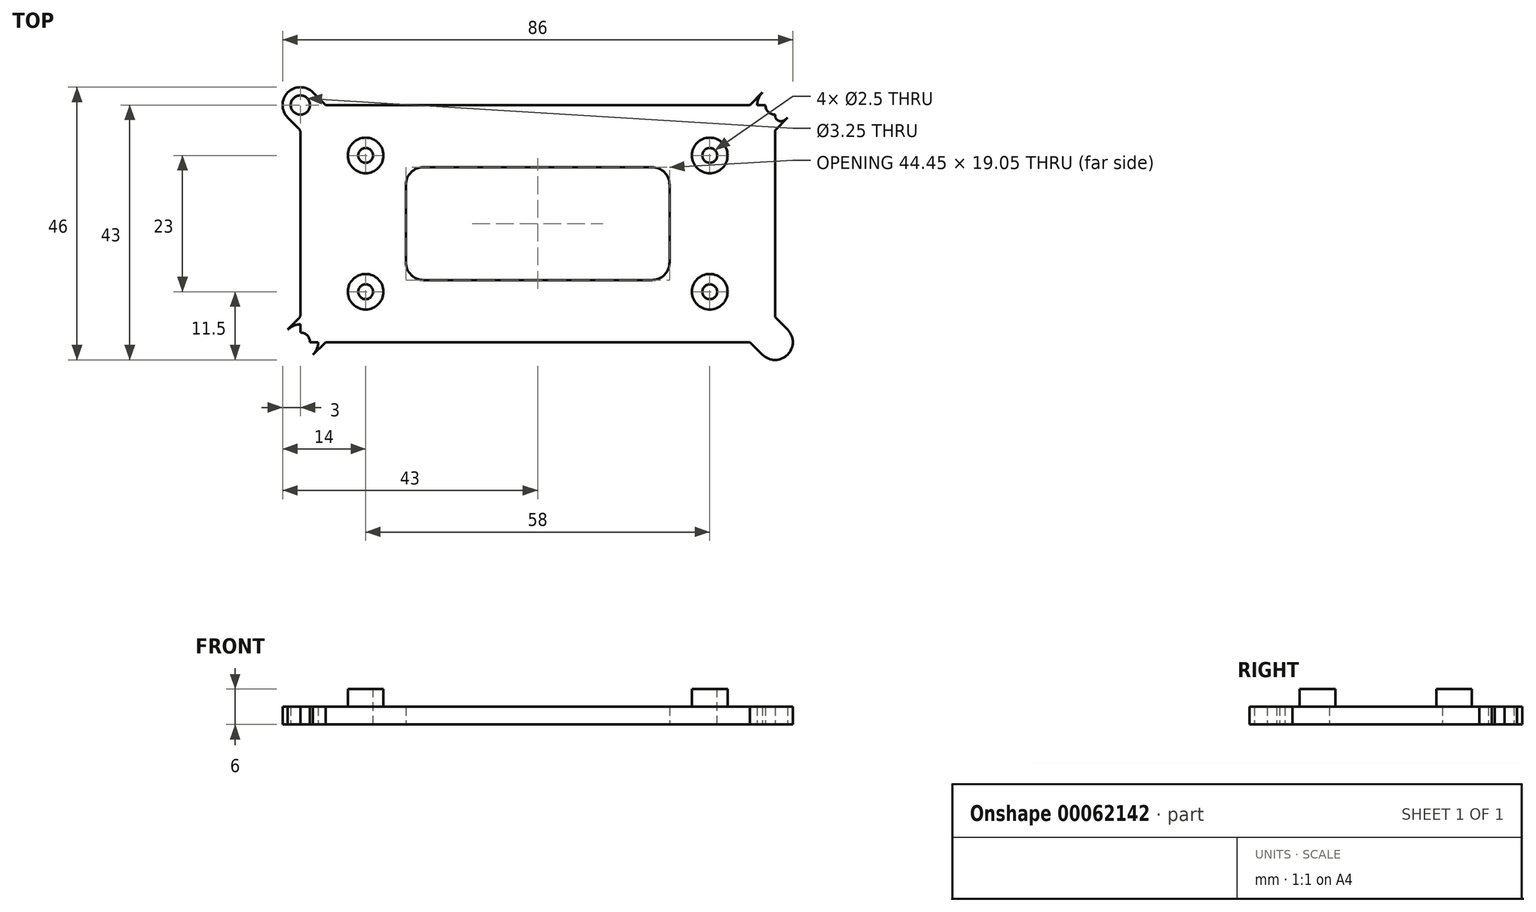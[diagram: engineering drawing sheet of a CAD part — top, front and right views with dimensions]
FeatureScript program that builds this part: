
annotation { "Feature Type Name" : "Feature", "Feature Type Description" : "" }
export const myFeature = defineFeature(function(context is Context, id is Id, definition is map)
    precondition{}
    {
        {
            var Q0;
            Q0=qCreatedBy(makeId("Top.planeOp"),FACE);
            var sketch = newSketch(context, id + "F0", { "sketchPlane" : qUnion([Q0])});
            skLineSegment(sketch, "E0.bottom", {"start": v(-40, 20) * mm, "end": v(40, 20) * mm});
            skLineSegment(sketch, "E0.top", {"start": v(-40, -20) * mm, "end": v(40, -20) * mm});
            skLineSegment(sketch, "E0.left", {"start": v(-40, 20) * mm, "end": v(-40, -20) * mm});
            skLineSegment(sketch, "E0.right", {"start": v(40, 20) * mm, "end": v(40, -20) * mm});
            skSolve(sketch);
        }
        {
            var Q0;
            Q0=makeQuery(id+"F0.imprint","IMPRINT",FACE,{"disambiguationData":[TD([[makeQuery(id+"F0.imprint","IMPRINT",EDGE,{"derivedFrom":sQuery(id+"F0.wireOp",EDGE,"E0.bottom")}),-1.0]])]});
            extrude(context, id + "F1", {"entities" : qUnion([Q0]), "depth" : 3 * mm});
        }
        {
            var Q0;
            Q0=makeQuery(id+"F1.opExtrude","CAP_FACE",FACE,{"disambiguationData":[OSD([sQuery(id+"F0.wireOp",EDGE,"E0.bottom"),sQuery(id+"F0.wireOp",EDGE,"E0.top"),sQuery(id+"F0.wireOp",EDGE,"E0.left"),sQuery(id+"F0.wireOp",EDGE,"E0.right")])],"isStart":false});
            var sketch = newSketch(context, id + "F2", { "sketchPlane" : qUnion([Q0])});
            skCircle(sketch, "E1", {"center": v(-29, -11.5) * mm, "radius": 3 * mm});
            skCircle(sketch, "E2", {"center": v(29, -11.5) * mm, "radius": 3 * mm});
            skCircle(sketch, "E3", {"center": v(29, 11.5) * mm, "radius": 3 * mm});
            skCircle(sketch, "E4", {"center": v(-29, 11.5) * mm, "radius": 3 * mm});
            skSolve(sketch);
        }
        {
            var Q0;
            Q0=makeQuery(id+"F2.imprint","IMPRINT",FACE,{"disambiguationData":[TD([[makeQuery(id+"F2.imprint","IMPRINT",EDGE,{"derivedFrom":sQuery(id+"F2.wireOp",EDGE,"E4")}),1.0]])]});
            var Q1;
            Q1=makeQuery(id+"F2.imprint","IMPRINT",FACE,{"disambiguationData":[TD([[makeQuery(id+"F2.imprint","IMPRINT",EDGE,{"derivedFrom":sQuery(id+"F2.wireOp",EDGE,"E3")}),1.0]])]});
            var Q2;
            Q2=makeQuery(id+"F2.imprint","IMPRINT",FACE,{"disambiguationData":[TD([[makeQuery(id+"F2.imprint","IMPRINT",EDGE,{"derivedFrom":sQuery(id+"F2.wireOp",EDGE,"E2")}),1.0]])]});
            var Q3;
            Q3=makeQuery(id+"F2.imprint","IMPRINT",FACE,{"disambiguationData":[TD([[makeQuery(id+"F2.imprint","IMPRINT",EDGE,{"derivedFrom":sQuery(id+"F2.wireOp",EDGE,"E1")}),1.0]])]});
            extrude(context, id + "F3", {"entities" : qUnion([Q0, Q1, Q2, Q3]), "operationType" : NewBodyOperationType.ADD, "depth" : 3 * mm});
        }
        {
            var Q0;
            Q0=makeQuery(id+"F3.opExtrude","CAP_FACE",FACE,{"disambiguationData":[OSD([sQuery(id+"F2.wireOp",EDGE,"E3")])],"isStart":false});
            var sketch = newSketch(context, id + "F4", { "sketchPlane" : qUnion([Q0])});
            skCircle(sketch, "E5.0", {"center": v(-29, 11.5) * mm, "radius": 3 * mm});
            skCircle(sketch, "E5.1", {"center": v(29, 11.5) * mm, "radius": 3 * mm});
            skCircle(sketch, "E5.2", {"center": v(29, -11.5) * mm, "radius": 3 * mm});
            skCircle(sketch, "E5.3", {"center": v(-29, -11.5) * mm, "radius": 3 * mm});
            skSolve(sketch);
        }
        {
            var Q0;
            Q0=sQuery(id+"F4.wireOp",VERTEX,"E5.0.center");
            var Q1;
            Q1=sQuery(id+"F4.wireOp",VERTEX,"E5.1.center");
            var Q2;
            Q2=sQuery(id+"F4.wireOp",VERTEX,"E5.2.center");
            var Q3;
            Q3=sQuery(id+"F4.wireOp",VERTEX,"E5.3.center");
            var Q4;
            Q4=makeQuery(id+"F1.opExtrude","SWEPT_BODY",BODY,{"disambiguationData":[OSD([sQuery(id+"F0.wireOp",EDGE,"E0.bottom"),sQuery(id+"F0.wireOp",EDGE,"E0.top"),sQuery(id+"F0.wireOp",EDGE,"E0.left"),sQuery(id+"F0.wireOp",EDGE,"E0.right")])]});
            hole(context, id + "F5", {"style" : HoleStyle.SIMPLE, "holeDiameter" : 2.5 * mm, "endStyle" : HoleEndStyle.THROUGH, "locations" : qUnion([Q0, Q1, Q2, Q3]), "scope" : qUnion([Q4])});
        }
        {
            var Q0;
            Q0=makeQuery(id+"F1.opExtrude","CAP_FACE",FACE,{"disambiguationData":[OSD([sQuery(id+"F0.wireOp",EDGE,"E0.bottom"),sQuery(id+"F0.wireOp",EDGE,"E0.top"),sQuery(id+"F0.wireOp",EDGE,"E0.left"),sQuery(id+"F0.wireOp",EDGE,"E0.right")])],"isStart":true});
            var sketch = newSketch(context, id + "F6", { "sketchPlane" : qUnion([Q0])});
            skCircle(sketch, "E6", {"center": v(40, 20) * mm, "radius": 3 * mm});
            skLineSegment(sketch, "E7", {"start": v(37.88, 22.12) * mm, "end": v(35.76, 20) * mm});
            skLineSegment(sketch, "E8", {"start": v(42.12, 17.88) * mm, "end": v(40, 15.76) * mm});
            skLineSegment(sketch, "E9.MirrorCS", {"start": v(37.88, -22.12) * mm, "end": v(35.76, -20) * mm});
            skLineSegment(sketch, "E10.MirrorCS", {"start": v(42.12, -17.88) * mm, "end": v(40, -15.76) * mm});
            skCircle(sketch, "E11.MirrorC", {"center": v(40, -20) * mm, "radius": 3 * mm});
            skLineSegment(sketch, "E12.MirrorCS", {"start": v(-37.88, -22.12) * mm, "end": v(-35.76, -20) * mm});
            skCircle(sketch, "E13.MirrorC", {"center": v(-40, -20) * mm, "radius": 3 * mm});
            skLineSegment(sketch, "E14.MirrorCS", {"start": v(-42.12, -17.88) * mm, "end": v(-40, -15.76) * mm});
            skLineSegment(sketch, "E15.MirrorCS", {"start": v(-42.12, 17.88) * mm, "end": v(-40, 15.76) * mm});
            skLineSegment(sketch, "E16.MirrorCS", {"start": v(-37.88, 22.12) * mm, "end": v(-35.76, 20) * mm});
            skCircle(sketch, "E17.MirrorC", {"center": v(-40, 20) * mm, "radius": 3 * mm});
            skSolve(sketch);
        }
        {
            var Q0;
            {var subQ0=sQuery(id+"F6.wireOp",EDGE,"E6");var subQ1=makeQuery(id+"F6.imprint","INTERSECT",VERTEX,{"derivedFrom":[subQ0,sQuery(id+"F6.wireOp",EDGE,"soFXJ1EB-8HO6-MR9N-8HIc-to1pPQWrAkPu")]});Q0=makeQuery(id+"F6.imprint","IMPRINT",FACE,{"disambiguationData":[TD([[makeQuery(id+"F6.imprint","IMPRINT",EDGE,{"disambiguationData":[TD([[subQ1,-1.0]])],"derivedFrom":subQ0}),1.0]])]});}
            var Q1;
            {var subQ0=sQuery(id+"F6.wireOp",EDGE,"soFXJ1EB-8HO6-MR9N-8HIc-to1pPQWrAkPu");Q1=makeQuery(id+"F6.imprint","IMPRINT",FACE,{"disambiguationData":[TD([[makeQuery(id+"F6.imprint","IMPRINT",EDGE,{"derivedFrom":subQ0}),1.0]])]});}
            var Q2;
            {var subQ0=sQuery(id+"F6.wireOp",EDGE,"Z4YqX5LU-mUXy-Cds5-Czo9-QNd9TRQbJKcO");Q2=makeQuery(id+"F6.imprint","IMPRINT",FACE,{"disambiguationData":[TD([[makeQuery(id+"F6.imprint","IMPRINT",EDGE,{"derivedFrom":subQ0}),-1.0]])]});}
            var Q3;
            {var subQ0=sQuery(id+"F6.wireOp",EDGE,"a5341563-2c41-44e3-9b47-e9f27f0d3a280.MirrorC");var subQ1=makeQuery(id+"F6.imprint","INTERSECT",VERTEX,{"derivedFrom":[sQuery(id+"F6.wireOp",EDGE,"0210edd8-b347-4c23-a09a-b419c3a22fa00.MirrorCS"),subQ0]});Q3=makeQuery(id+"F6.imprint","IMPRINT",FACE,{"disambiguationData":[TD([[makeQuery(id+"F6.imprint","IMPRINT",EDGE,{"disambiguationData":[TD([[subQ1,-1.0]])],"derivedFrom":subQ0}),-1.0]])]});}
            var Q4;
            {var subQ0=sQuery(id+"F6.wireOp",EDGE,"0210edd8-b347-4c23-a09a-b419c3a22fa00.MirrorCS");Q4=makeQuery(id+"F6.imprint","IMPRINT",FACE,{"disambiguationData":[TD([[makeQuery(id+"F6.imprint","IMPRINT",EDGE,{"derivedFrom":subQ0}),-1.0]])]});}
            var Q5;
            {var subQ0=sQuery(id+"F6.wireOp",EDGE,"2f044340-a0b1-4631-b95b-f2c242ba9c770.MirrorCS");Q5=makeQuery(id+"F6.imprint","IMPRINT",FACE,{"disambiguationData":[TD([[makeQuery(id+"F6.imprint","IMPRINT",EDGE,{"derivedFrom":subQ0}),1.0]])]});}
            var Q6;
            {var subQ0=sQuery(id+"F6.wireOp",EDGE,"2f99d0b1-1a89-4974-9a16-afa06d6dc4af0.MirrorC");var subQ1=makeQuery(id+"F6.imprint","INTERSECT",VERTEX,{"derivedFrom":[subQ0,sQuery(id+"F6.wireOp",EDGE,"bc17fd96-254d-4ff9-a344-3499c0479a8f0.MirrorCS")]});Q6=makeQuery(id+"F6.imprint","IMPRINT",FACE,{"disambiguationData":[TD([[makeQuery(id+"F6.imprint","IMPRINT",EDGE,{"disambiguationData":[TD([[subQ1,-1.0]])],"derivedFrom":subQ0}),1.0]])]});}
            var Q7;
            {var subQ0=sQuery(id+"F6.wireOp",EDGE,"f0ec589f-6775-499c-a41f-7fb6111fc43a0.MirrorCS");Q7=makeQuery(id+"F6.imprint","IMPRINT",FACE,{"disambiguationData":[TD([[makeQuery(id+"F6.imprint","IMPRINT",EDGE,{"derivedFrom":subQ0}),-1.0]])]});}
            var Q8;
            {var subQ0=sQuery(id+"F6.wireOp",EDGE,"bc17fd96-254d-4ff9-a344-3499c0479a8f0.MirrorCS");Q8=makeQuery(id+"F6.imprint","IMPRINT",FACE,{"disambiguationData":[TD([[makeQuery(id+"F6.imprint","IMPRINT",EDGE,{"derivedFrom":subQ0}),1.0]])]});}
            var Q9;
            {var subQ0=sQuery(id+"F6.wireOp",EDGE,"94c3390e-faa4-4edb-91fe-58140658a5c30.MirrorC");var subQ1=makeQuery(id+"F6.imprint","INTERSECT",VERTEX,{"derivedFrom":[subQ0,sQuery(id+"F6.wireOp",EDGE,"4ec94b05-feb2-45ef-b047-bc99985147690.MirrorCS")]});Q9=makeQuery(id+"F6.imprint","IMPRINT",FACE,{"disambiguationData":[TD([[makeQuery(id+"F6.imprint","IMPRINT",EDGE,{"disambiguationData":[TD([[subQ1,-1.0]])],"derivedFrom":subQ0}),-1.0]])]});}
            var Q10;
            {var subQ0=sQuery(id+"F6.wireOp",EDGE,"213ae7a3-055c-491c-8cde-c86d012d92890.MirrorCS");Q10=makeQuery(id+"F6.imprint","IMPRINT",FACE,{"disambiguationData":[TD([[makeQuery(id+"F6.imprint","IMPRINT",EDGE,{"derivedFrom":subQ0}),1.0]])]});}
            var Q11;
            {var subQ0=sQuery(id+"F6.wireOp",EDGE,"4ec94b05-feb2-45ef-b047-bc99985147690.MirrorCS");Q11=makeQuery(id+"F6.imprint","IMPRINT",FACE,{"disambiguationData":[TD([[makeQuery(id+"F6.imprint","IMPRINT",EDGE,{"derivedFrom":subQ0}),-1.0]])]});}
            var Q12;
            {var subQ3=sQuery(id+"F6.wireOp",EDGE,"E17.MirrorC");var subQ6=makeQuery(id+"F6.imprint","INTERSECT",VERTEX,{"derivedFrom":[sQuery(id+"F6.wireOp",EDGE,"E16.MirrorCS"),subQ3]});Q12=makeQuery(id+"F6.imprint","IMPRINT",FACE,{"disambiguationData":[TD([[makeQuery(id+"F6.imprint","IMPRINT",EDGE,{"disambiguationData":[TD([[subQ6,-1.0]])],"derivedFrom":subQ3}),-1.0]])]});}
            var Q13;
            {var subQ0=sQuery(id+"F6.wireOp",EDGE,"E16.MirrorCS");Q13=makeQuery(id+"F6.imprint","IMPRINT",FACE,{"disambiguationData":[TD([[makeQuery(id+"F6.imprint","IMPRINT",EDGE,{"derivedFrom":subQ0}),-1.0]])]});}
            var Q14;
            {var subQ0=sQuery(id+"F6.wireOp",EDGE,"E15.MirrorCS");Q14=makeQuery(id+"F6.imprint","IMPRINT",FACE,{"disambiguationData":[TD([[makeQuery(id+"F6.imprint","IMPRINT",EDGE,{"derivedFrom":subQ0}),1.0]])]});}
            var Q15;
            {var subQ0=sQuery(id+"F6.wireOp",EDGE,"E13.MirrorC");var subQ1=makeQuery(id+"F6.imprint","INTERSECT",VERTEX,{"derivedFrom":[sQuery(id+"F6.wireOp",EDGE,"E12.MirrorCS"),subQ0]});Q15=makeQuery(id+"F6.imprint","IMPRINT",FACE,{"disambiguationData":[TD([[makeQuery(id+"F6.imprint","IMPRINT",EDGE,{"disambiguationData":[TD([[subQ1,-1.0]])],"derivedFrom":subQ0}),1.0]])]});}
            var Q16;
            {var subQ0=sQuery(id+"F6.wireOp",EDGE,"E14.MirrorCS");Q16=makeQuery(id+"F6.imprint","IMPRINT",FACE,{"disambiguationData":[TD([[makeQuery(id+"F6.imprint","IMPRINT",EDGE,{"derivedFrom":subQ0}),-1.0]])]});}
            var Q17;
            {var subQ0=sQuery(id+"F6.wireOp",EDGE,"E12.MirrorCS");Q17=makeQuery(id+"F6.imprint","IMPRINT",FACE,{"disambiguationData":[TD([[makeQuery(id+"F6.imprint","IMPRINT",EDGE,{"derivedFrom":subQ0}),1.0]])]});}
            var Q18;
            {var subQ3=sQuery(id+"F6.wireOp",EDGE,"E11.MirrorC");var subQ7=makeQuery(id+"F6.imprint","INTERSECT",VERTEX,{"derivedFrom":[sQuery(id+"F6.wireOp",EDGE,"E9.MirrorCS"),subQ3]});Q18=makeQuery(id+"F6.imprint","IMPRINT",FACE,{"disambiguationData":[TD([[makeQuery(id+"F6.imprint","IMPRINT",EDGE,{"disambiguationData":[TD([[subQ7,-1.0]])],"derivedFrom":subQ3}),-1.0]])]});}
            var Q19;
            {var subQ0=sQuery(id+"F6.wireOp",EDGE,"E10.MirrorCS");Q19=makeQuery(id+"F6.imprint","IMPRINT",FACE,{"disambiguationData":[TD([[makeQuery(id+"F6.imprint","IMPRINT",EDGE,{"derivedFrom":subQ0}),1.0]])]});}
            var Q20;
            {var subQ0=sQuery(id+"F6.wireOp",EDGE,"E9.MirrorCS");Q20=makeQuery(id+"F6.imprint","IMPRINT",FACE,{"disambiguationData":[TD([[makeQuery(id+"F6.imprint","IMPRINT",EDGE,{"derivedFrom":subQ0}),-1.0]])]});}
            var Q21;
            {var subQ0=sQuery(id+"F6.wireOp",EDGE,"E8");Q21=makeQuery(id+"F6.imprint","IMPRINT",FACE,{"disambiguationData":[TD([[makeQuery(id+"F6.imprint","IMPRINT",EDGE,{"derivedFrom":subQ0}),-1.0]])]});}
            var Q22;
            {var subQ0=sQuery(id+"F6.wireOp",EDGE,"E7");Q22=makeQuery(id+"F6.imprint","IMPRINT",FACE,{"disambiguationData":[TD([[makeQuery(id+"F6.imprint","IMPRINT",EDGE,{"derivedFrom":subQ0}),1.0]])]});}
            extrude(context, id + "F7", {"entities" : qUnion([Q0, Q1, Q2, Q3, Q4, Q5, Q6, Q7, Q8, Q9, Q10, Q11, Q12, Q13, Q14, Q15, Q16, Q17, Q18, Q19, Q20, Q21, Q22]), "operationType" : NewBodyOperationType.ADD, "oppositeDirection" : true, "depth" : 3 * mm});
        }
        {
            var Q0;
            {var subQ0=sQuery(id+"F0.wireOp",EDGE,"E0.left");var subQ1=sQuery(id+"F0.wireOp",EDGE,"E0.right");Q0=makeQuery(id+"F7.boolean.opBoolean","MERGE",FACE,{"derivedFrom":[makeQuery(id+"F1.opExtrude","CAP_FACE",FACE,{"disambiguationData":[OSD([sQuery(id+"F0.wireOp",EDGE,"E0.bottom"),sQuery(id+"F0.wireOp",EDGE,"E0.top"),subQ0,subQ1])],"isStart":true}),makeQuery(id+"F7.opExtrude","CAP_FACE",FACE,{"disambiguationData":[OSD([subQ1,sQuery(id+"F6.wireOp",EDGE,"E6"),sQuery(id+"F6.wireOp",EDGE,"soFXJ1EB-8HO6-MR9N-8HIc-to1pPQWrAkPu"),sQuery(id+"F6.wireOp",EDGE,"Z4YqX5LU-mUXy-Cds5-Czo9-QNd9TRQbJKcO")])],"isStart":true}),makeQuery(id+"F7.opExtrude","CAP_FACE",FACE,{"disambiguationData":[OSD([subQ1,sQuery(id+"F6.wireOp",EDGE,"213ae7a3-055c-491c-8cde-c86d012d92890.MirrorCS"),sQuery(id+"F6.wireOp",EDGE,"94c3390e-faa4-4edb-91fe-58140658a5c30.MirrorC"),sQuery(id+"F6.wireOp",EDGE,"4ec94b05-feb2-45ef-b047-bc99985147690.MirrorCS")])],"isStart":true}),makeQuery(id+"F7.opExtrude","CAP_FACE",FACE,{"disambiguationData":[OSD([subQ0,sQuery(id+"F6.wireOp",EDGE,"0210edd8-b347-4c23-a09a-b419c3a22fa00.MirrorCS"),sQuery(id+"F6.wireOp",EDGE,"2f044340-a0b1-4631-b95b-f2c242ba9c770.MirrorCS"),sQuery(id+"F6.wireOp",EDGE,"a5341563-2c41-44e3-9b47-e9f27f0d3a280.MirrorC")])],"isStart":true}),makeQuery(id+"F7.opExtrude","CAP_FACE",FACE,{"disambiguationData":[OSD([subQ0,sQuery(id+"F6.wireOp",EDGE,"f0ec589f-6775-499c-a41f-7fb6111fc43a0.MirrorCS"),sQuery(id+"F6.wireOp",EDGE,"2f99d0b1-1a89-4974-9a16-afa06d6dc4af0.MirrorC"),sQuery(id+"F6.wireOp",EDGE,"bc17fd96-254d-4ff9-a344-3499c0479a8f0.MirrorCS")])],"isStart":true})]});}
            var sketch = newSketch(context, id + "F8", { "sketchPlane" : qUnion([Q0])});
            skLineSegment(sketch, "E18.3", {"start": v(37.88, 22.12) * mm, "end": v(37.88, 22.12) * mm});
            skArc(sketch, "E19.0", {"start": v(-42.12, 17.88) * mm, "mid": v(-42.12, 22.12) * mm, "end": v(-37.88, 22.12) * mm});
            skArc(sketch, "E19.1", {"start": v(-42.12, -17.88) * mm, "mid": v(-42.12, -22.12) * mm, "end": v(-37.88, -22.12) * mm});
            skArc(sketch, "E19.2", {"start": v(42.12, -17.88) * mm, "mid": v(42.12, -22.12) * mm, "end": v(37.88, -22.12) * mm});
            skSolve(sketch);
        }
        {
            var Q0;
            Q0=sQuery(id+"F8.wireOp",VERTEX,"E18.0.center");
            var Q1;
            Q1=sQuery(id+"F8.wireOp",VERTEX,"E18.1.center");
            var Q2;
            Q2=sQuery(id+"F8.wireOp",VERTEX,"E18.2.center");
            var Q3;
            Q3=sQuery(id+"F8.wireOp",VERTEX,"E18.3.center");
            var Q4;
            Q4=sQuery(id+"F8.wireOp",VERTEX,"E19.0.center");
            var Q5;
            Q5=sQuery(id+"F8.wireOp",VERTEX,"E19.1.center");
            var Q6;
            Q6=sQuery(id+"F8.wireOp",VERTEX,"E19.2.center");
            var Q7;
            Q7=makeQuery(id+"F1.opExtrude","SWEPT_BODY",BODY,{"disambiguationData":[OSD([sQuery(id+"F0.wireOp",EDGE,"E0.bottom"),sQuery(id+"F0.wireOp",EDGE,"E0.top"),sQuery(id+"F0.wireOp",EDGE,"E0.left"),sQuery(id+"F0.wireOp",EDGE,"E0.right")])]});
            hole(context, id + "F9", {"style" : HoleStyle.SIMPLE, "holeDiameter" : 3.25 * mm, "endStyle" : HoleEndStyle.THROUGH, "locations" : qUnion([Q0, Q1, Q2, Q3, Q4, Q5, Q6]), "scope" : qUnion([Q7])});
        }
        {
            var Q0;
            {var subQ0=sQuery(id+"F0.wireOp",EDGE,"E0.left");var subQ1=sQuery(id+"F0.wireOp",EDGE,"E0.right");Q0=makeQuery(id+"F7.boolean.opBoolean","MERGE",FACE,{"derivedFrom":[makeQuery(id+"F1.opExtrude","CAP_FACE",FACE,{"disambiguationData":[OSD([sQuery(id+"F0.wireOp",EDGE,"E0.bottom"),sQuery(id+"F0.wireOp",EDGE,"E0.top"),subQ0,subQ1])],"isStart":true}),makeQuery(id+"F7.opExtrude","CAP_FACE",FACE,{"disambiguationData":[OSD([subQ1,sQuery(id+"F6.wireOp",EDGE,"E6"),sQuery(id+"F6.wireOp",EDGE,"soFXJ1EB-8HO6-MR9N-8HIc-to1pPQWrAkPu"),sQuery(id+"F6.wireOp",EDGE,"Z4YqX5LU-mUXy-Cds5-Czo9-QNd9TRQbJKcO")])],"isStart":true}),makeQuery(id+"F7.opExtrude","CAP_FACE",FACE,{"disambiguationData":[OSD([subQ1,sQuery(id+"F6.wireOp",EDGE,"213ae7a3-055c-491c-8cde-c86d012d92890.MirrorCS"),sQuery(id+"F6.wireOp",EDGE,"94c3390e-faa4-4edb-91fe-58140658a5c30.MirrorC"),sQuery(id+"F6.wireOp",EDGE,"4ec94b05-feb2-45ef-b047-bc99985147690.MirrorCS")])],"isStart":true}),makeQuery(id+"F7.opExtrude","CAP_FACE",FACE,{"disambiguationData":[OSD([subQ0,sQuery(id+"F6.wireOp",EDGE,"0210edd8-b347-4c23-a09a-b419c3a22fa00.MirrorCS"),sQuery(id+"F6.wireOp",EDGE,"2f044340-a0b1-4631-b95b-f2c242ba9c770.MirrorCS"),sQuery(id+"F6.wireOp",EDGE,"a5341563-2c41-44e3-9b47-e9f27f0d3a280.MirrorC")])],"isStart":true}),makeQuery(id+"F7.opExtrude","CAP_FACE",FACE,{"disambiguationData":[OSD([subQ0,sQuery(id+"F6.wireOp",EDGE,"f0ec589f-6775-499c-a41f-7fb6111fc43a0.MirrorCS"),sQuery(id+"F6.wireOp",EDGE,"2f99d0b1-1a89-4974-9a16-afa06d6dc4af0.MirrorC"),sQuery(id+"F6.wireOp",EDGE,"bc17fd96-254d-4ff9-a344-3499c0479a8f0.MirrorCS")])],"isStart":true})]});}
            var sketch = newSketch(context, id + "F10", { "sketchPlane" : qUnion([Q0])});
            skLineSegment(sketch, "E20.bottom", {"start": v(-22.23, 9.53) * mm, "end": v(22.23, 9.52) * mm});
            skLineSegment(sketch, "E20.top", {"start": v(-22.23, -9.53) * mm, "end": v(22.23, -9.53) * mm});
            skLineSegment(sketch, "E20.left", {"start": v(-22.23, 9.53) * mm, "end": v(-22.23, -9.53) * mm});
            skLineSegment(sketch, "E20.right", {"start": v(22.23, 9.53) * mm, "end": v(22.23, -9.53) * mm});
            skSolve(sketch);
        }
        {
            var Q0;
            Q0=makeQuery(id+"F10.imprint","IMPRINT",FACE,{"disambiguationData":[TD([[makeQuery(id+"F10.imprint","IMPRINT",EDGE,{"derivedFrom":sQuery(id+"F10.wireOp",EDGE,"E20.bottom")}),-1.0]])]});
            extrude(context, id + "F11", {"entities" : qUnion([Q0]), "operationType" : NewBodyOperationType.REMOVE, "endBound" : BoundingType.THROUGH_ALL, "oppositeDirection" : true, "depth" : 25.4 * mm});
        }
        {
            var Q0;
            Q0=makeQuery(id+"F11.boolean.opBoolean","COPY",EDGE,{"derivedFrom":makeQuery(id+"F11.opExtrude","SWEPT_EDGE",EDGE,{"disambiguationData":[OSD([sQuery(id+"F10.wireOp",EDGE,"E20.top"),sQuery(id+"F10.wireOp",EDGE,"E20.left")])]})});
            var Q1;
            Q1=makeQuery(id+"F11.boolean.opBoolean","COPY",EDGE,{"derivedFrom":makeQuery(id+"F11.opExtrude","SWEPT_EDGE",EDGE,{"disambiguationData":[OSD([sQuery(id+"F10.wireOp",EDGE,"E20.bottom"),sQuery(id+"F10.wireOp",EDGE,"E20.right")])]})});
            var Q2;
            Q2=makeQuery(id+"F11.boolean.opBoolean","COPY",EDGE,{"derivedFrom":makeQuery(id+"F11.opExtrude","SWEPT_EDGE",EDGE,{"disambiguationData":[OSD([sQuery(id+"F10.wireOp",EDGE,"E20.bottom"),sQuery(id+"F10.wireOp",EDGE,"E20.left")])]})});
            var Q3;
            Q3=makeQuery(id+"F11.boolean.opBoolean","COPY",EDGE,{"derivedFrom":makeQuery(id+"F11.opExtrude","SWEPT_EDGE",EDGE,{"disambiguationData":[OSD([sQuery(id+"F10.wireOp",EDGE,"E20.top"),sQuery(id+"F10.wireOp",EDGE,"E20.right")])]})});
            fillet(context, id + "F12", {"entities" : qUnion([Q0, Q1, Q2, Q3]), "radius" : 3 * mm, "tangentPropagation" : true, "allowEdgeOverflow" : false});
        }
        {
            var Q0;
            Q0=makeQuery(id+"F7.opExtrude","SWEPT_EDGE",EDGE,{"disambiguationData":[OSD([sQuery(id+"F0.wireOp",EDGE,"E0.left"),sQuery(id+"F6.wireOp",EDGE,"2f044340-a0b1-4631-b95b-f2c242ba9c770.MirrorCS")])]});
            var Q1;
            Q1=makeQuery(id+"F7.opExtrude","SWEPT_EDGE",EDGE,{"disambiguationData":[OSD([sQuery(id+"F0.wireOp",EDGE,"E0.right"),sQuery(id+"F6.wireOp",EDGE,"Z4YqX5LU-mUXy-Cds5-Czo9-QNd9TRQbJKcO")])]});
            var Q2;
            Q2=makeQuery(id+"F7.opExtrude","SWEPT_EDGE",EDGE,{"disambiguationData":[OSD([sQuery(id+"F0.wireOp",EDGE,"E0.right"),sQuery(id+"F6.wireOp",EDGE,"213ae7a3-055c-491c-8cde-c86d012d92890.MirrorCS")])]});
            var Q3;
            Q3=makeQuery(id+"F7.opExtrude","SWEPT_EDGE",EDGE,{"disambiguationData":[OSD([sQuery(id+"F0.wireOp",EDGE,"E0.left"),sQuery(id+"F6.wireOp",EDGE,"f0ec589f-6775-499c-a41f-7fb6111fc43a0.MirrorCS")])]});
            fillet(context, id + "F13", {"entities" : qUnion([Q0, Q1, Q2, Q3]), "radius" : 1 * mm, "tangentPropagation" : true, "allowEdgeOverflow" : false});
        }
    });
